# Revit family: URBANE II UNIVERSAL RAIL SHOWER 800MM
name_source: partatom
category: Plumbing Fixtures
units: mm (PartAtom-declared; Revit-internal decimal feet)

## family parameters
Cut with Voids When Loaded = No
Host = Face
OmniClass Number = 23.45.05.14.17
OmniClass Title = Showers
Part Type = Normal
Room Calculation Point = No
Round Connector Dimension = Use Diameter
Shared = No

## types (5) — shared parameters
CW Connection = Yes
HW Connection = Yes
Manufacturer = GWA Bathrooms & Kitchens
Material_Face = GWA-Plastic-General
Material_Sprays = GWA-Plastic-General
URL = https://www.caroma.com.au
Vent Connection = No
Waste Connection = No
zero-valued in all types: Default Elevation

## per-type parameters (varying)
| type | Material | Model |
| URBANE II UNIVERSAL RAIL SHOWER 800MM - CHROME | GWA_Metal-Chrome | 96331C4E |
| URBANE II UNIVERSAL RAIL SHOWER 800MM - BLACK | GWA-Metal-Black | 96331B4E |
| URBANE II UNIVERSAL RAIL SHOWER 800MM - BRUSHED BRASS | GWA_Metal-Brushed-Brass | 96331BB4E |
| URBANE II UNIVERSAL RAIL SHOWER 800MM - GUN METAL | GWA-Metal-Gunmetal Grey | 96331GM4E |
| URBANE II UNIVERSAL RAIL SHOWER 800MM - BRUSHED NICKEL | GWA_Metal-Brushed-Nickel | 96331BN4E |

note: column(s) folded — value = type name in every type: Description

## geometry (parser evidence)
native form markers: Sweep x6
no freeform markers — native parametric forms only
